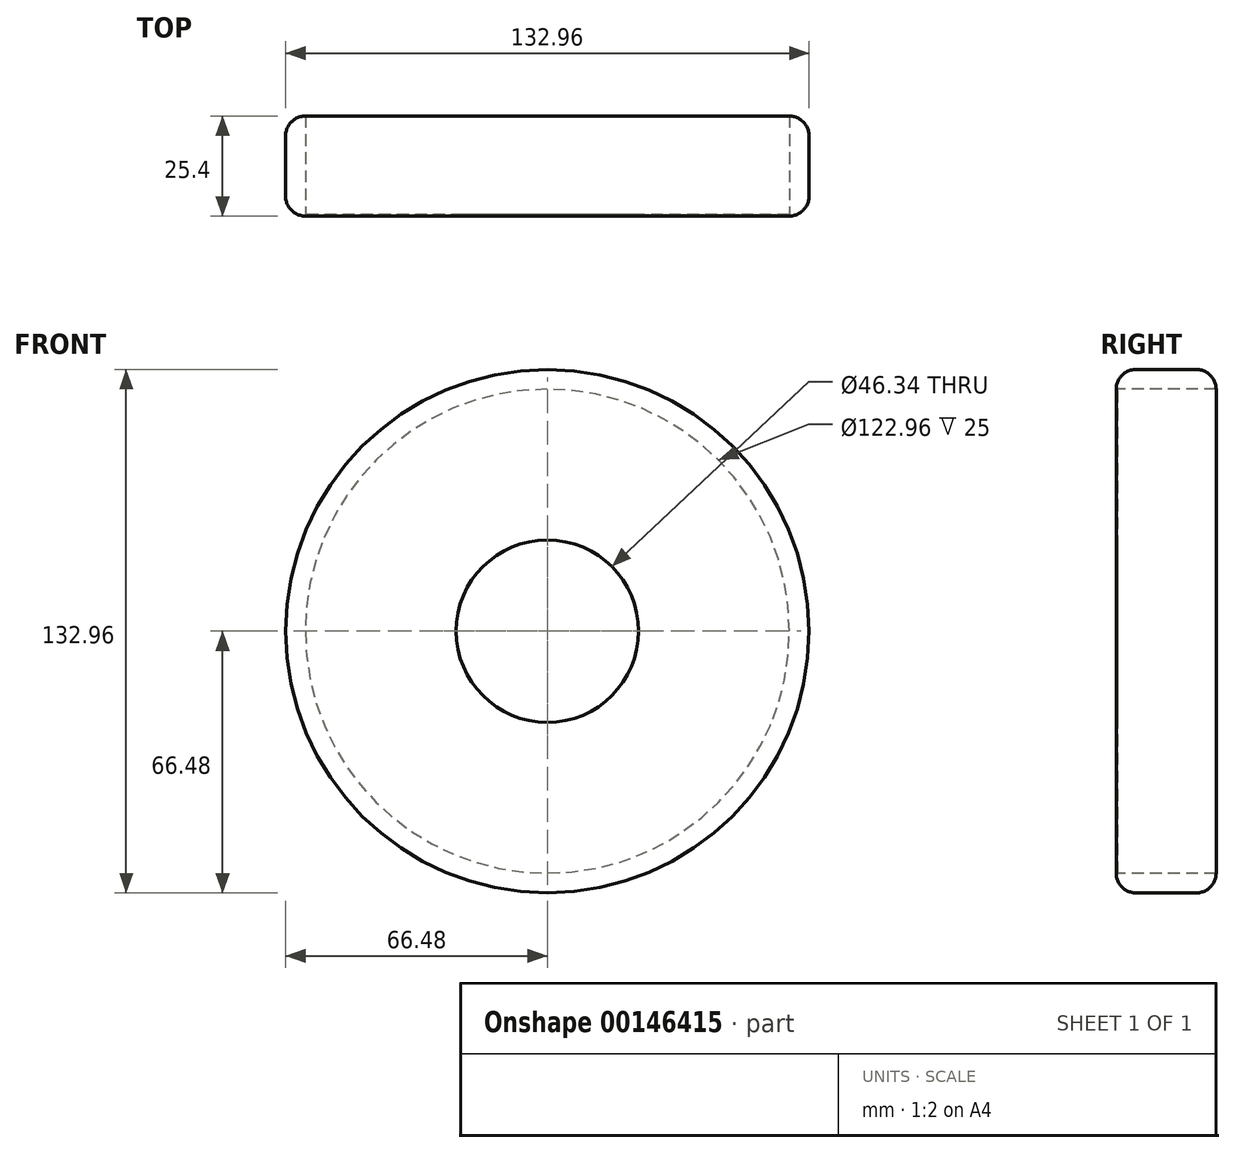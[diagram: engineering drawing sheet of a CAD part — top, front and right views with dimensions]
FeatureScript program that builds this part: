
annotation { "Feature Type Name" : "Feature", "Feature Type Description" : "" }
export const myFeature = defineFeature(function(context is Context, id is Id, definition is map)
    precondition{}
    {
        {
            var Q0;
            Q0=qCreatedBy(makeId("Front.planeOp"),FACE);
            var sketch = newSketch(context, id + "F0", { "sketchPlane" : qUnion([Q0])});
            skCircle(sketch, "E0", {"center": v(0, 0) * mm, "radius": 66.48 * mm});
            skSolve(sketch);
        }
        {
            var Q0;
            Q0=makeQuery(id+"F0.imprint","IMPRINT",FACE,{"disambiguationData":[TD([[makeQuery(id+"F0.imprint","IMPRINT",EDGE,{"derivedFrom":sQuery(id+"F0.wireOp",EDGE,"E0")}),1.0]])]});
            extrude(context, id + "F1", {"entities" : qUnion([Q0]), "depth" : 25.4 * mm});
        }
        {
            var Q0;
            Q0=makeQuery(id+"F1.opExtrude","CAP_EDGE",EDGE,{"disambiguationData":[OSD([sQuery(id+"F0.wireOp",EDGE,"E0")])],"isStart":false});
            var Q1;
            Q1=makeQuery(id+"F1.opExtrude","CAP_EDGE",EDGE,{"disambiguationData":[OSD([sQuery(id+"F0.wireOp",EDGE,"E0")])],"isStart":true});
            fillet(context, id + "F2", {"entities" : qUnion([Q0, Q1]), "radius" : 5 * mm, "tangentPropagation" : true, "allowEdgeOverflow" : false});
        }
        {
            var Q0;
            Q0=makeQuery(id+"F1.opExtrude","CAP_FACE",FACE,{"disambiguationData":[OSD([sQuery(id+"F0.wireOp",EDGE,"E0")])],"isStart":false});
            var sketch = newSketch(context, id + "F3", { "sketchPlane" : qUnion([Q0])});
            skCircle(sketch, "E1", {"center": v(0, 0) * mm, "radius": 23.17 * mm});
            skSolve(sketch);
        }
        {
            var Q0;
            Q0=makeQuery(id+"F3.imprint","IMPRINT",FACE,{"disambiguationData":[TD([[makeQuery(id+"F3.imprint","IMPRINT",EDGE,{"derivedFrom":sQuery(id+"F3.wireOp",EDGE,"E1")}),1.0]])]});
            var Q1;
            Q1=makeQuery(id+"F1.opExtrude","CAP_FACE",FACE,{"disambiguationData":[OSD([sQuery(id+"F0.wireOp",EDGE,"E0")])],"isStart":true});
            extrude(context, id + "F4", {"entities" : qUnion([Q0, Q1]), "operationType" : NewBodyOperationType.REMOVE, "oppositeDirection" : true, "depth" : 25 * mm, "hasSecondDirection" : true, "secondDirectionOppositeDirection" : false, "secondDirectionDepth" : 25 * mm});
        }
    });
